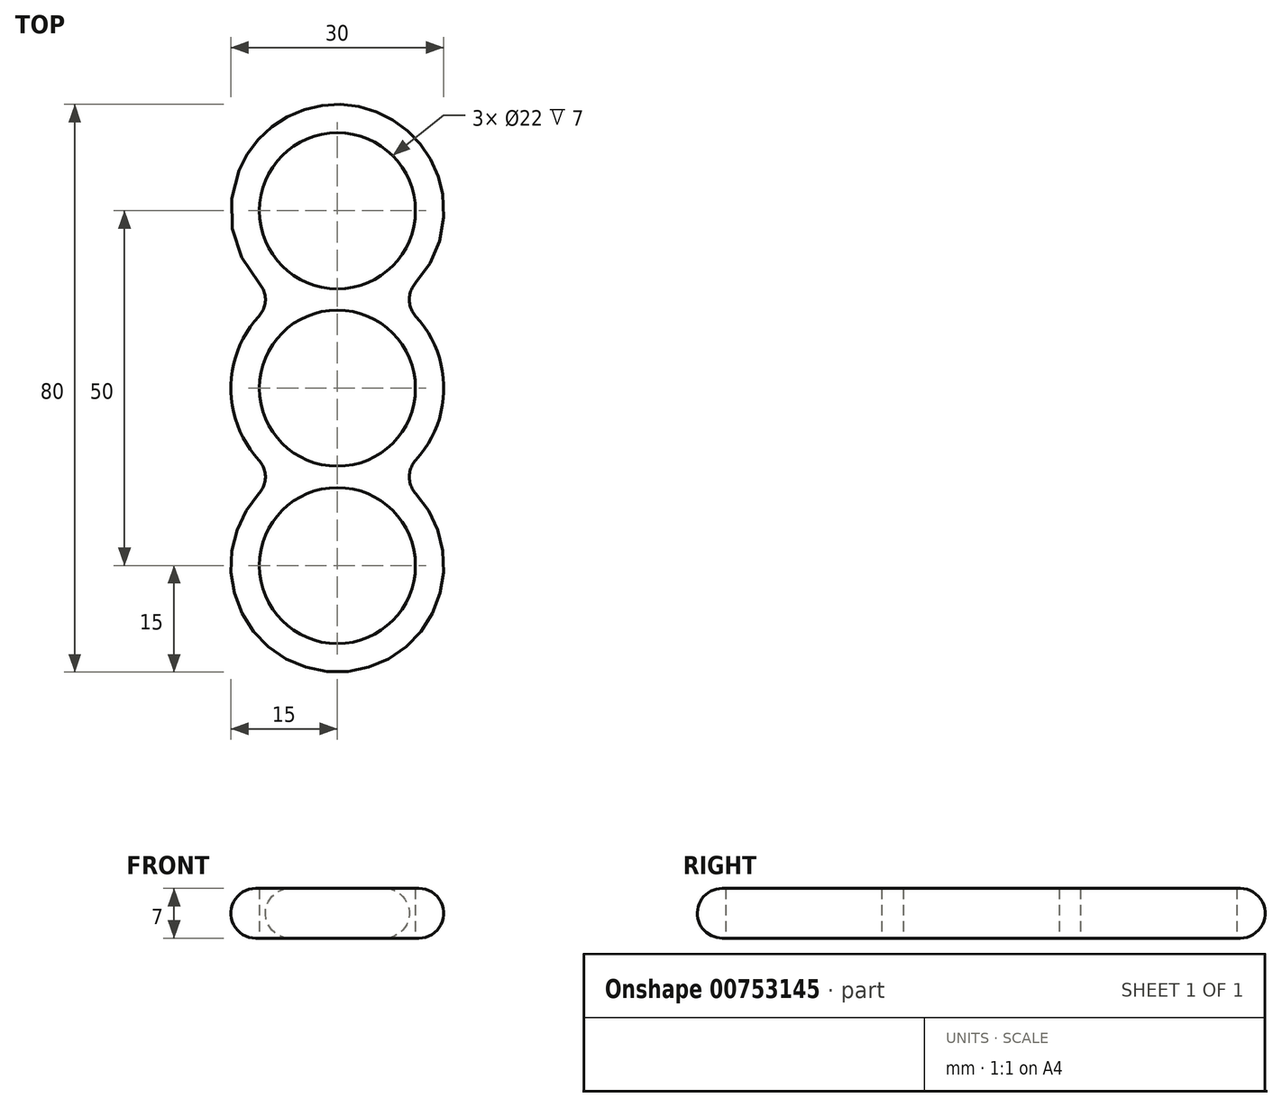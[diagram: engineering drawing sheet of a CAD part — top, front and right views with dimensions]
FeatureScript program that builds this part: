
annotation { "Feature Type Name" : "Feature", "Feature Type Description" : "" }
export const myFeature = defineFeature(function(context is Context, id is Id, definition is map)
    precondition{}
    {
        {
            var Q0;
            Q0=qCreatedBy(makeId("Top.planeOp"),FACE);
            var sketch = newSketch(context, id + "F0", { "sketchPlane" : qUnion([Q0])});
            skCircle(sketch, "E0", {"center": v(0, 0) * mm, "radius": 11 * mm});
            skArc(sketch, "E1", {"start": v(11.06, 14.86) * mm, "mid": v(8.34, 37.47) * mm, "end": v(-13.6, 31.35) * mm});
            skArc(sketch, "E2", {"start": v(-11.06, 10.14) * mm, "mid": v(-15, 0) * mm, "end": v(-11.06, -10.14) * mm});
            skArc(sketch, "E3", {"start": v(-11.06, -14.86) * mm, "mid": v(-14.99, -24.34) * mm, "end": v(-11.9, -34.13) * mm});
            skArc(sketch, "E4.trimOffspring", {"start": v(11.06, -10.14) * mm, "mid": v(15, 0) * mm, "end": v(11.06, 10.14) * mm});
            skPoint(sketch, "E5.visualSharp", {"position": v(8.3, 12.5) * mm});
            skArc(sketch, "E5.filletArc", {"start": v(11.06, 14.86) * mm, "mid": v(10.14, 12.5) * mm, "end": v(11.06, 10.14) * mm});
            skPoint(sketch, "E6.visualSharp", {"position": v(-8.3, 12.5) * mm});
            skArc(sketch, "E6.filletArc", {"start": v(-11.06, 10.14) * mm, "mid": v(-10.14, 12.5) * mm, "end": v(-11.06, 14.86) * mm});
            skPoint(sketch, "E7.visualSharp", {"position": v(-8.3, -12.5) * mm});
            skArc(sketch, "E7.filletArc", {"start": v(-11.06, -14.86) * mm, "mid": v(-10.14, -12.5) * mm, "end": v(-11.06, -10.14) * mm});
            skPoint(sketch, "E8.visualSharp", {"position": v(8.3, -12.5) * mm});
            skArc(sketch, "E8.filletArc", {"start": v(11.06, -10.14) * mm, "mid": v(10.14, -12.5) * mm, "end": v(11.06, -14.86) * mm});
            skArc(sketch, "E9.trimOffspring", {"start": v(-11.9, -34.13) * mm, "mid": v(9.64, -36.5) * mm, "end": v(11.06, -14.86) * mm});
            skArc(sketch, "E10.trimOffspring", {"start": v(-13.6, 31.35) * mm, "mid": v(-14.83, 22.72) * mm, "end": v(-11.06, 14.86) * mm});
            skCircle(sketch, "E11.converted", {"center": v(0, 25) * mm, "radius": 11 * mm});
            skCircle(sketch, "E12.converted", {"center": v(0, -25) * mm, "radius": 11 * mm});
            skSolve(sketch);
        }
        {
            var Q0;
            Q0=qSketchRegion(id+"F0",true);
            extrude(context, id + "F1", {"entities" : qUnion([Q0]), "depth" : 7 * mm, "offsetDistance" : 25 * mm});
        }
        {
            var Q0;
            Q0=makeQuery(id+"F1.opExtrude","CAP_EDGE",EDGE,{"disambiguationData":[OSD([sQuery(id+"F0.wireOp",EDGE,"E1")])],"isStart":false});
            var Q1;
            Q1=makeQuery(id+"F1.opExtrude","CAP_EDGE",EDGE,{"disambiguationData":[OSD([sQuery(id+"F0.wireOp",EDGE,"E1")])],"isStart":true});
            fillet(context, id + "F2", {"entities" : qUnion([Q0, Q1]), "radius" : 3.5 * mm, "tangentPropagation" : true, "allowEdgeOverflow" : false});
        }
    });
